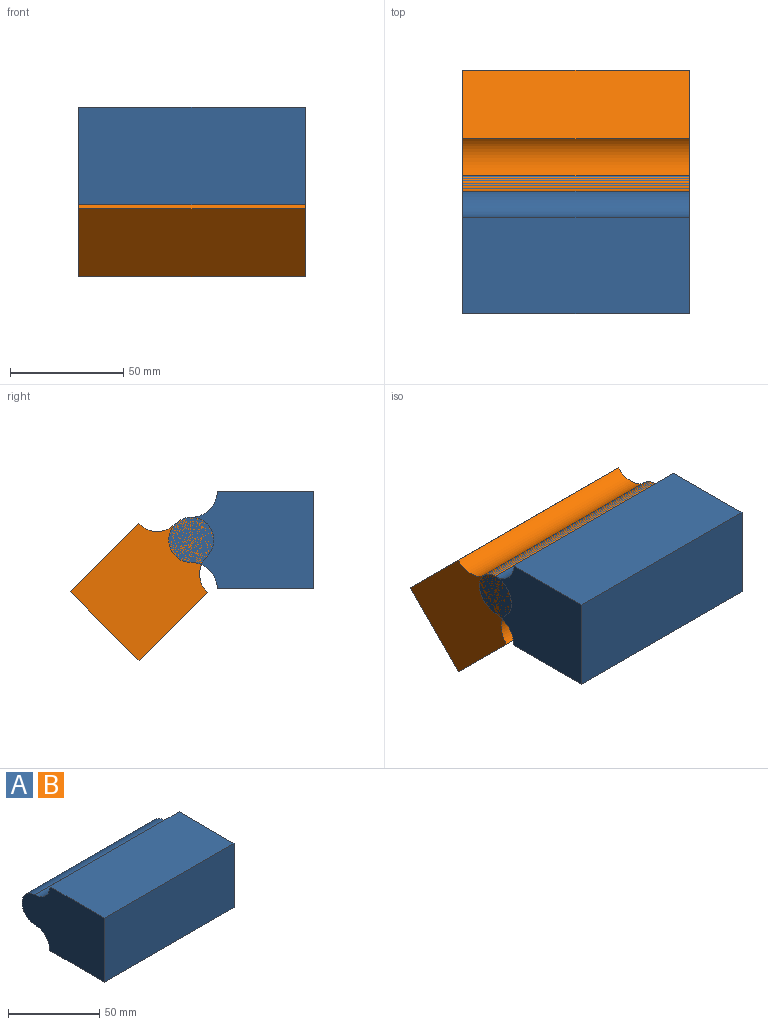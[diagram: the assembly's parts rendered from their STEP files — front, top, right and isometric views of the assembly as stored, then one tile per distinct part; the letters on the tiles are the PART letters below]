
ASSEMBLY  parts=2 mates=1
PART A: 8 faces, bbox 100x64x42.9 mm
  f0: plane 100x42.87mm, normal (0,-1,0), area 4287mm2, adj f1,f5,f6,f7
  f1: plane 100x42.52mm, normal (0,0,-1), area 4251.9mm2, adj f0,f2,f6,f7
  f2: cylinder r=11.43mm len=100mm, axis (-1,0,0), area 1796.2mm2, adj f1,f3,f6,f7
  f3: cylinder r=10mm len=100mm, axis (-1,0,0), area 3141.6mm2, adj f2,f4,f6,f7
  f4: cylinder r=11.43mm len=100mm, axis (-1,0,0), area 1796.2mm2, adj f3,f5,f6,f7
  f5: plane 100x42.52mm, normal (0,0,1), area 4251.9mm2, adj f0,f4,f6,f7
  f6: plane 63.95x42.87mm, normal (1,0,0), area 2264.7mm2, adj f0,f1,f2,f3,f4,f5
  f7: plane 63.95x42.87mm, normal (-1,0,0), area 2264.7mm2, adj f0,f1,f2,f3,f4,f5
PART B: same geometry as A
PLACE A at identity fixed
PLACE B rot(axis=(0,0.38,0.92),180deg) t=(0,0,0)mm
MATE revolute A.f3 <-> B.f3  axis (-1,0,0) through (0,0,0)mm
